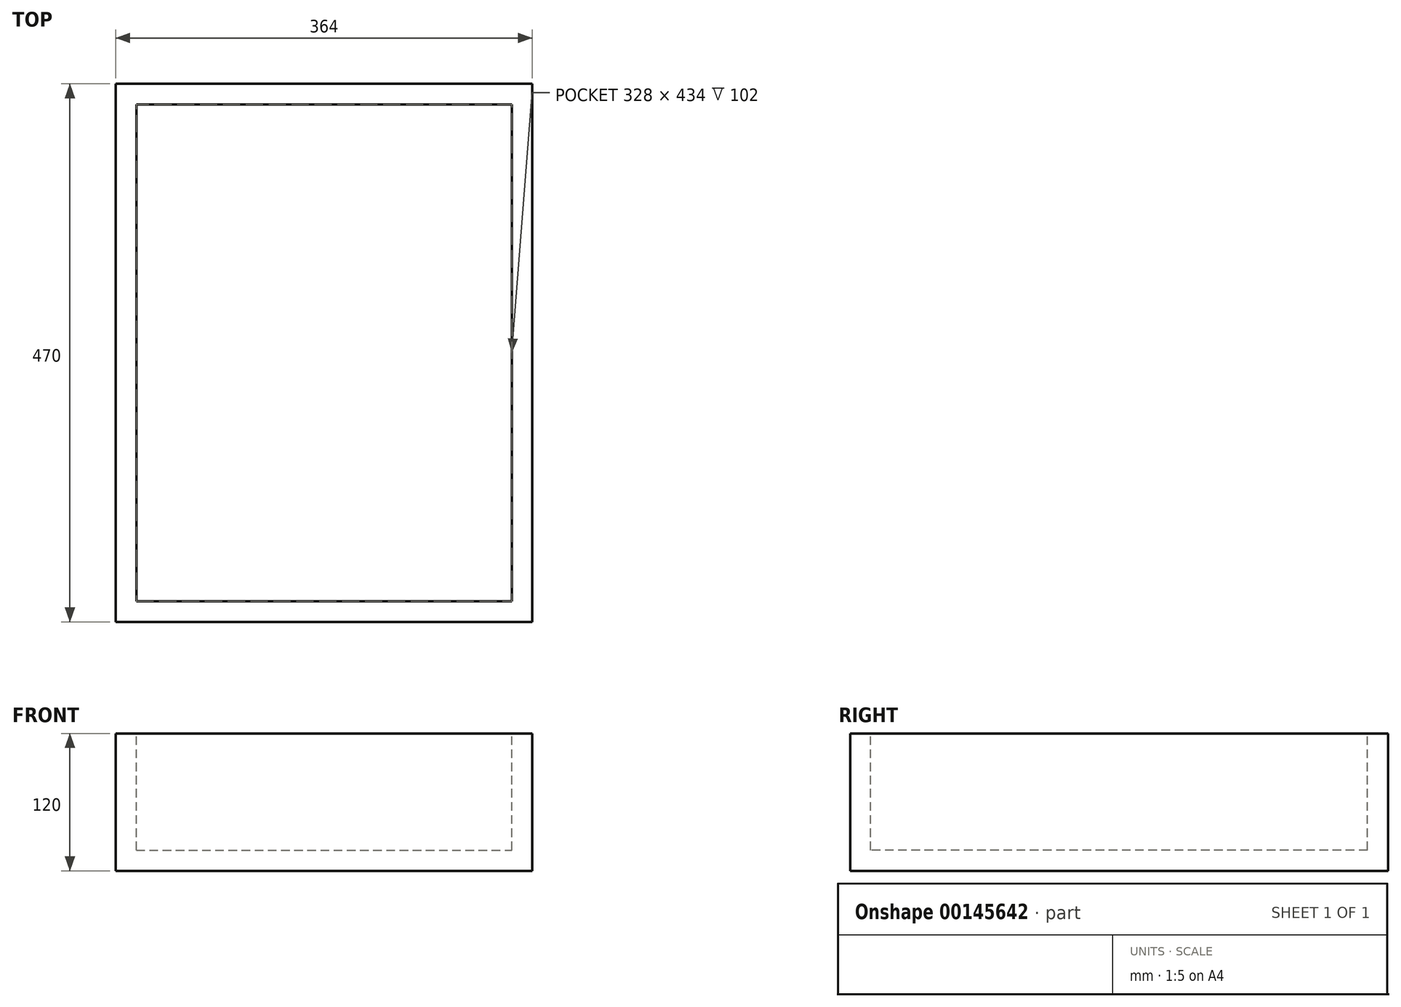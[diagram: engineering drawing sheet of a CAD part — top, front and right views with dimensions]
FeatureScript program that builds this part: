
annotation { "Feature Type Name" : "Feature", "Feature Type Description" : "" }
export const myFeature = defineFeature(function(context is Context, id is Id, definition is map)
    precondition{}
    {
        {
            var Q0;
            Q0=qCreatedBy(makeId("Top.planeOp"),FACE);
            var sketch = newSketch(context, id + "F0", { "sketchPlane" : qUnion([Q0])});
            skLineSegment(sketch, "E0.bottom", {"start": v(182, -235) * mm, "end": v(-182, -235) * mm});
            skLineSegment(sketch, "E0.top", {"start": v(182, 235) * mm, "end": v(-182, 235) * mm});
            skLineSegment(sketch, "E0.left", {"start": v(182, -235) * mm, "end": v(182, 235) * mm});
            skLineSegment(sketch, "E0.right", {"start": v(-182, -235) * mm, "end": v(-182, 235) * mm});
            skPoint(sketch, "E0.middle", {"position": v(0, 0) * mm});
            skSolve(sketch);
        }
        {
            var Q0;
            Q0=makeQuery(id+"F0.imprint","IMPRINT",FACE,{"disambiguationData":[TD([[makeQuery(id+"F0.imprint","IMPRINT",EDGE,{"derivedFrom":sQuery(id+"F0.wireOp",EDGE,"E0.bottom")}),-1.0]])]});
            extrude(context, id + "F1", {"entities" : qUnion([Q0]), "endBound" : BoundingType.SYMMETRIC, "depth" : 120 * mm});
        }
        {
            var Q0;
            Q0=makeQuery(id+"F1.opExtrude","CAP_FACE",FACE,{"disambiguationData":[OSD([sQuery(id+"F0.wireOp",EDGE,"E0.bottom"),sQuery(id+"F0.wireOp",EDGE,"E0.top"),sQuery(id+"F0.wireOp",EDGE,"E0.left"),sQuery(id+"F0.wireOp",EDGE,"E0.right")])],"isStart":false});
            var sketch = newSketch(context, id + "F2", { "sketchPlane" : qUnion([Q0])});
            skLineSegment(sketch, "E1.0", {"start": v(-164, -217) * mm, "end": v(164, -217) * mm});
            skLineSegment(sketch, "E1.1", {"start": v(-164, 217) * mm, "end": v(-164, -217) * mm});
            skLineSegment(sketch, "E1.2", {"start": v(164, 217) * mm, "end": v(-164, 217) * mm});
            skLineSegment(sketch, "E1.3", {"start": v(164, -217) * mm, "end": v(164, 217) * mm});
            skSolve(sketch);
        }
        {
            var Q0;
            Q0=makeQuery(id+"F2.imprint","IMPRINT",FACE,{"disambiguationData":[TD([[makeQuery(id+"F2.imprint","IMPRINT",EDGE,{"derivedFrom":sQuery(id+"F2.wireOp",EDGE,"E1.0")}),1.0]])]});
            extrude(context, id + "F3", {"entities" : qUnion([Q0]), "operationType" : NewBodyOperationType.REMOVE, "oppositeDirection" : true, "depth" : 102 * mm});
        }
    });
